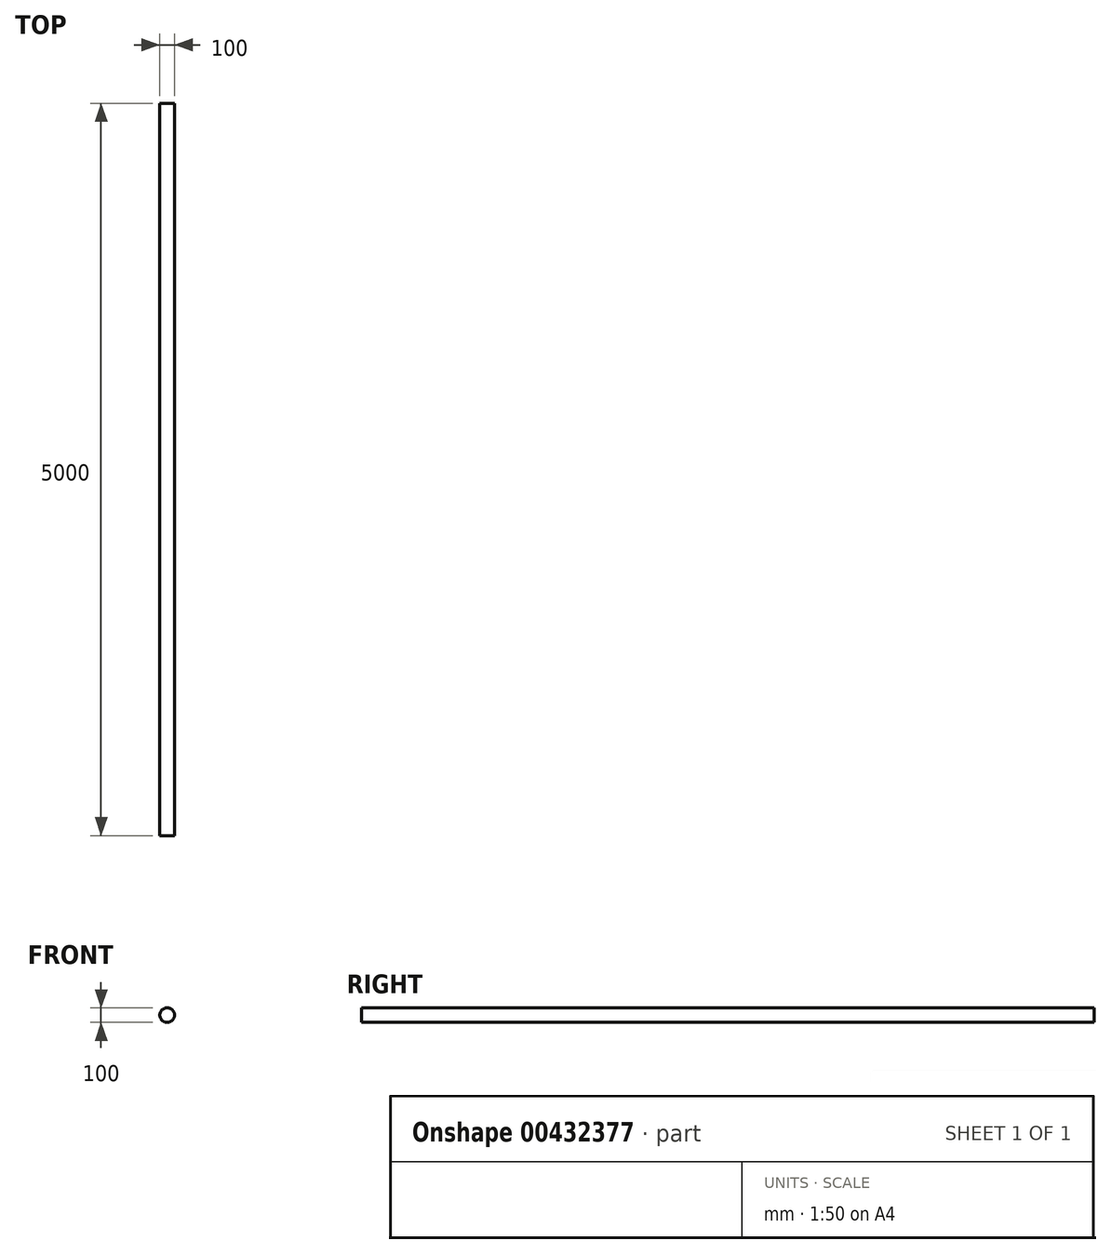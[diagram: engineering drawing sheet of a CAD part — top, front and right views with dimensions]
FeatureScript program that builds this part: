
annotation { "Feature Type Name" : "Feature", "Feature Type Description" : "" }
export const myFeature = defineFeature(function(context is Context, id is Id, definition is map)
    precondition{}
    {
        {
            var Q0;
            Q0=qCreatedBy(makeId("Front.planeOp"),FACE);
            var sketch = newSketch(context, id + "F0", { "sketchPlane" : qUnion([Q0])});
            skCircle(sketch, "E0", {"center": v(0, 0) * mm, "radius": 50 * mm});
            skSolve(sketch);
        }
        {
            var Q0;
            Q0=makeQuery(id+"F0.imprint","IMPRINT",FACE,{"disambiguationData":[TD([[makeQuery(id+"F0.imprint","IMPRINT",EDGE,{"derivedFrom":sQuery(id+"F0.wireOp",EDGE,"E0")}),1.0]])]});
            extrude(context, id + "F1", {"entities" : qUnion([Q0]), "depth" : 5000 * mm});
        }
    });
